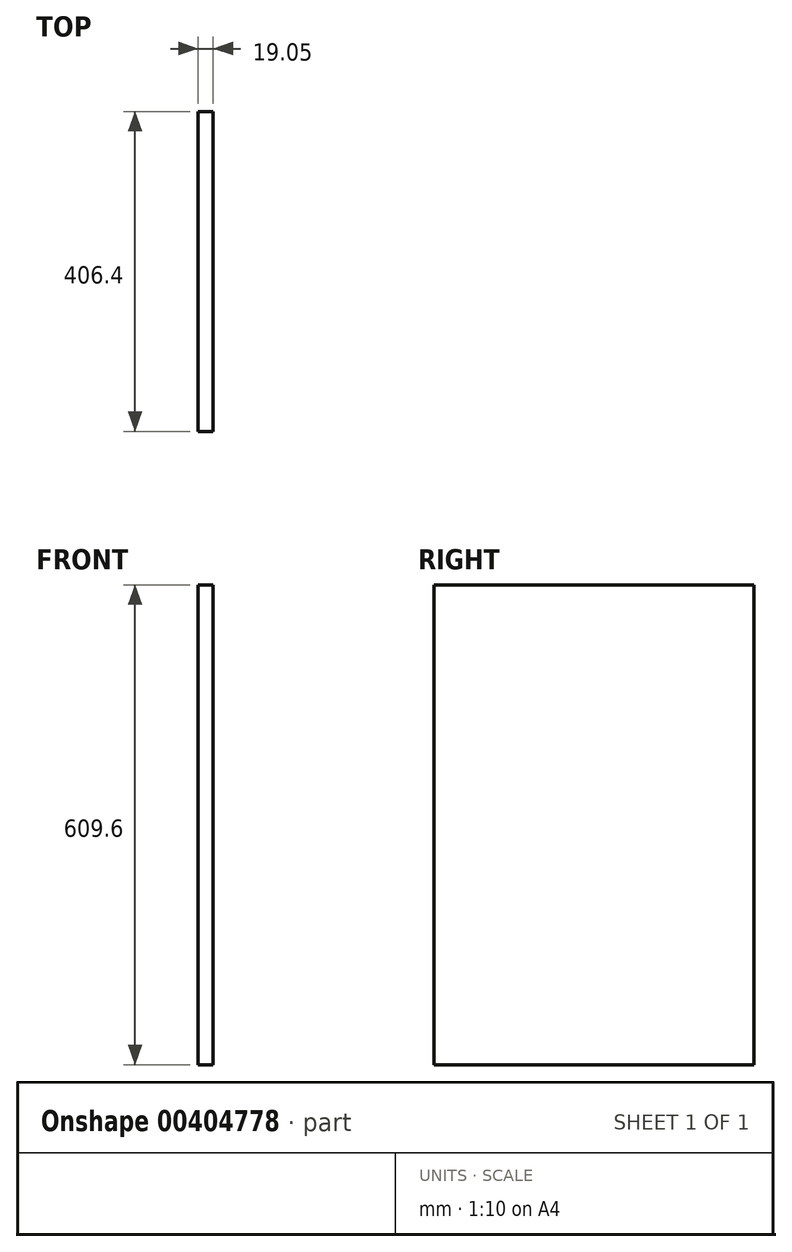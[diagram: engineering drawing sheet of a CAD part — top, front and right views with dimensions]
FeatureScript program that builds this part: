
annotation { "Feature Type Name" : "Feature", "Feature Type Description" : "" }
export const myFeature = defineFeature(function(context is Context, id is Id, definition is map)
    precondition{}
    {
        {
            var Q0;
            Q0=qCreatedBy(makeId("Right.planeOp"),FACE);
            var sketch = newSketch(context, id + "F0", { "sketchPlane" : qUnion([Q0])});
            skLineSegment(sketch, "E0.bottom", {"start": v(203.2, 304.8) * mm, "end": v(-203.2, 304.8) * mm});
            skLineSegment(sketch, "E0.top", {"start": v(203.2, -304.8) * mm, "end": v(-203.2, -304.8) * mm});
            skLineSegment(sketch, "E0.left", {"start": v(203.2, 304.8) * mm, "end": v(203.2, -304.8) * mm});
            skLineSegment(sketch, "E0.right", {"start": v(-203.2, 304.8) * mm, "end": v(-203.2, -304.8) * mm});
            skPoint(sketch, "E0.middle", {"position": v(0, 0) * mm});
            skSolve(sketch);
        }
        {
            var Q0;
            Q0 = qSketchRegion(id + "F0", true);
            extrude(context, id + "F1", {"entities" : qUnion([Q0]), "depth" : 19.05 * mm});
        }
    });
